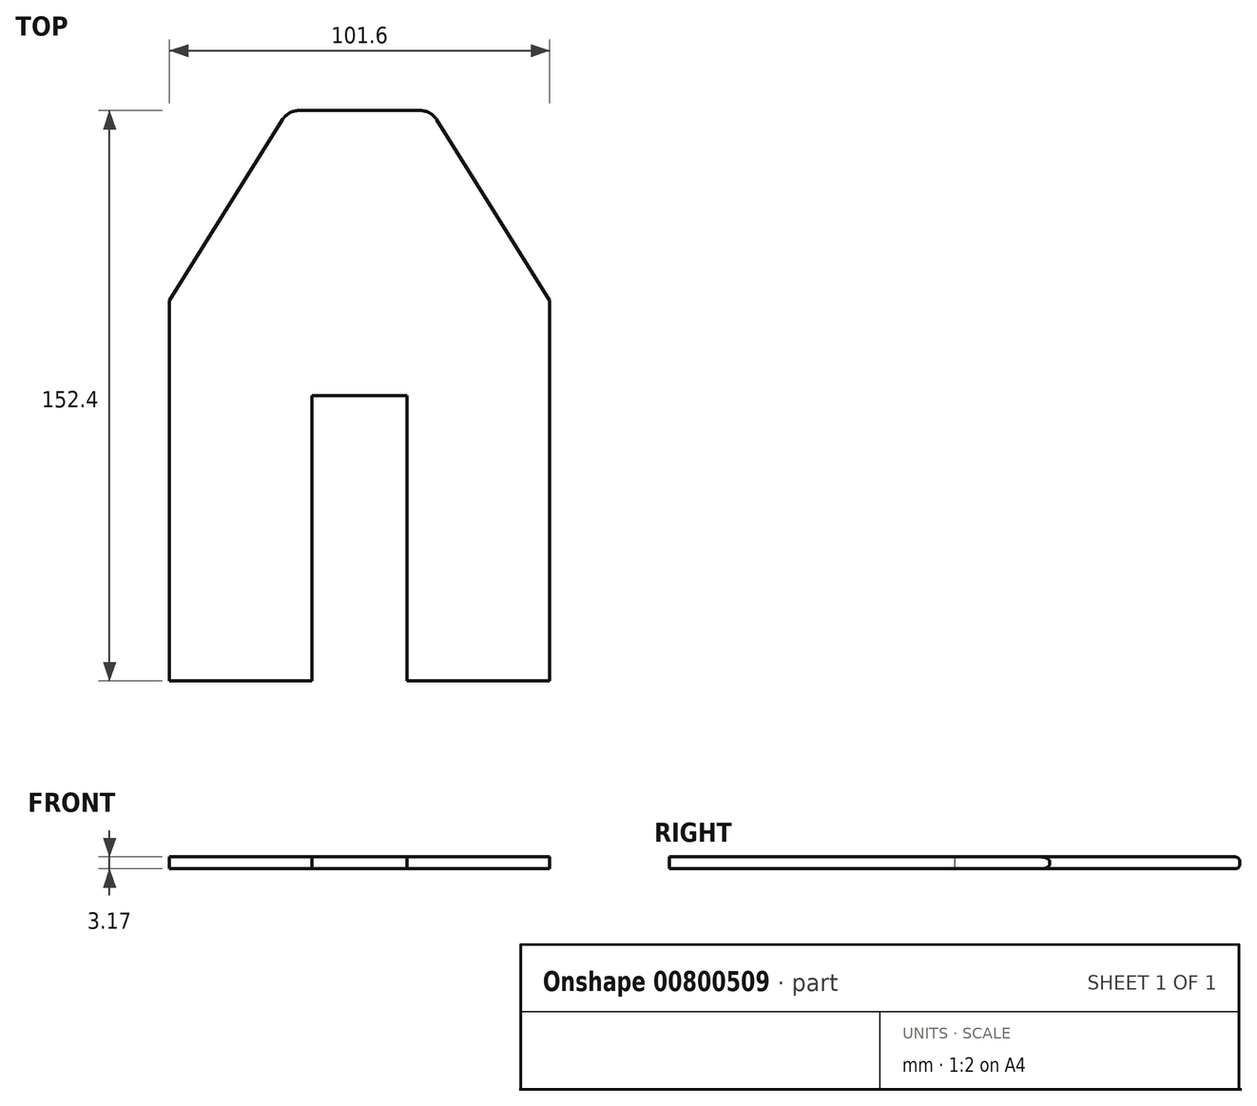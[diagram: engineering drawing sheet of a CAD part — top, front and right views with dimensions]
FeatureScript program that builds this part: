
annotation { "Feature Type Name" : "Feature", "Feature Type Description" : "" }
export const myFeature = defineFeature(function(context is Context, id is Id, definition is map)
    precondition{}
    {
        {
            var Q0;
            Q0=qCreatedBy(makeId("Top.planeOp"),FACE);
            var sketch = newSketch(context, id + "F0", { "sketchPlane" : qUnion([Q0])});
            skLineSegment(sketch, "E0.bottom", {"start": v(50.8, -76.2) * mm, "end": v(12.7, -76.2) * mm});
            skLineSegment(sketch, "E0.top", {"start": v(0, 76.2) * mm, "end": v(-19.05, 76.2) * mm});
            skLineSegment(sketch, "E0.left", {"start": v(50.8, -76.2) * mm, "end": v(50.8, 25.4) * mm});
            skLineSegment(sketch, "E0.right", {"start": v(-50.8, -76.2) * mm, "end": v(-50.8, 25.4) * mm});
            skPoint(sketch, "E0.middle", {"position": v(0, 0) * mm});
            skLineSegment(sketch, "E1.top", {"start": v(-12.7, 0) * mm, "end": v(12.7, 0) * mm});
            skLineSegment(sketch, "E1.left", {"start": v(-12.7, -76.2) * mm, "end": v(-12.7, 0) * mm});
            skLineSegment(sketch, "E1.right", {"start": v(12.7, -76.2) * mm, "end": v(12.7, 0) * mm});
            skLineSegment(sketch, "E2", {"start": v(0, 76.2) * mm, "end": v(19.05, 76.2) * mm});
            skLineSegment(sketch, "E3", {"start": v(-50.8, 25.4) * mm, "end": v(-19.05, 76.2) * mm});
            skLineSegment(sketch, "E4", {"start": v(50.8, 25.4) * mm, "end": v(19.05, 76.2) * mm});
            skPoint(sketch, "E5.orphan", {"position": v(50.8, 76.2) * mm});
            skPoint(sketch, "E6.orphan", {"position": v(-50.8, 76.2) * mm});
            skLineSegment(sketch, "E7.trimOffspring", {"start": v(-12.7, -76.2) * mm, "end": v(-50.8, -76.2) * mm});
            skPoint(sketch, "E8.start.orphan", {"position": v(0, -76.2) * mm});
            skSolve(sketch);
        }
        {
            var Q0;
            Q0=makeQuery(id+"F0.imprint","IMPRINT",FACE,{"disambiguationData":[TD([[makeQuery(id+"F0.imprint","IMPRINT",EDGE,{"derivedFrom":sQuery(id+"F0.wireOp",EDGE,"E0.bottom")}),-1.0]])]});
            extrude(context, id + "F1", {"entities" : qUnion([Q0]), "depth" : 3.17 * mm, "offsetDistance" : 25.4 * mm});
        }
        {
            var Q0;
            Q0=makeQuery(id+"F1.opExtrude","CAP_EDGE",EDGE,{"disambiguationData":[OSD([sQuery(id+"F0.wireOp",EDGE,"E4")])],"isStart":false});
            var Q1;
            Q1=makeQuery(id+"F1.opExtrude","CAP_EDGE",EDGE,{"disambiguationData":[OSD([sQuery(id+"F0.wireOp",EDGE,"E0.top"),sQuery(id+"F0.wireOp",EDGE,"E2")])],"isStart":false});
            var Q2;
            Q2=makeQuery(id+"F1.opExtrude","CAP_EDGE",EDGE,{"disambiguationData":[OSD([sQuery(id+"F0.wireOp",EDGE,"E3")])],"isStart":false});
            var Q3;
            Q3=makeQuery(id+"F1.opExtrude","CAP_EDGE",EDGE,{"disambiguationData":[OSD([sQuery(id+"F0.wireOp",EDGE,"E0.top"),sQuery(id+"F0.wireOp",EDGE,"E2")])],"isStart":true});
            var Q4;
            Q4=makeQuery(id+"F1.opExtrude","CAP_EDGE",EDGE,{"disambiguationData":[OSD([sQuery(id+"F0.wireOp",EDGE,"E4")])],"isStart":true});
            var Q5;
            Q5=makeQuery(id+"F1.opExtrude","CAP_EDGE",EDGE,{"disambiguationData":[OSD([sQuery(id+"F0.wireOp",EDGE,"E3")])],"isStart":true});
            fillet(context, id + "F2", {"entities" : qUnion([Q0, Q1, Q2, Q3, Q4, Q5]), "radius" : 1.27 * mm, "tangentPropagation" : true, "allowEdgeOverflow" : false});
        }
        {
            var Q0;
            Q0=makeQuery(id+"F1.opExtrude","SWEPT_EDGE",EDGE,{"disambiguationData":[OSD([sQuery(id+"F0.wireOp",EDGE,"E2"),sQuery(id+"F0.wireOp",EDGE,"E4")])]});
            var Q1;
            Q1=makeQuery(id+"F1.opExtrude","SWEPT_EDGE",EDGE,{"disambiguationData":[OSD([sQuery(id+"F0.wireOp",EDGE,"E0.top"),sQuery(id+"F0.wireOp",EDGE,"E3")])]});
            fillet(context, id + "F3", {"entities" : qUnion([Q0, Q1]), "radius" : 5.08 * mm, "tangentPropagation" : true, "allowEdgeOverflow" : false});
        }
    });
